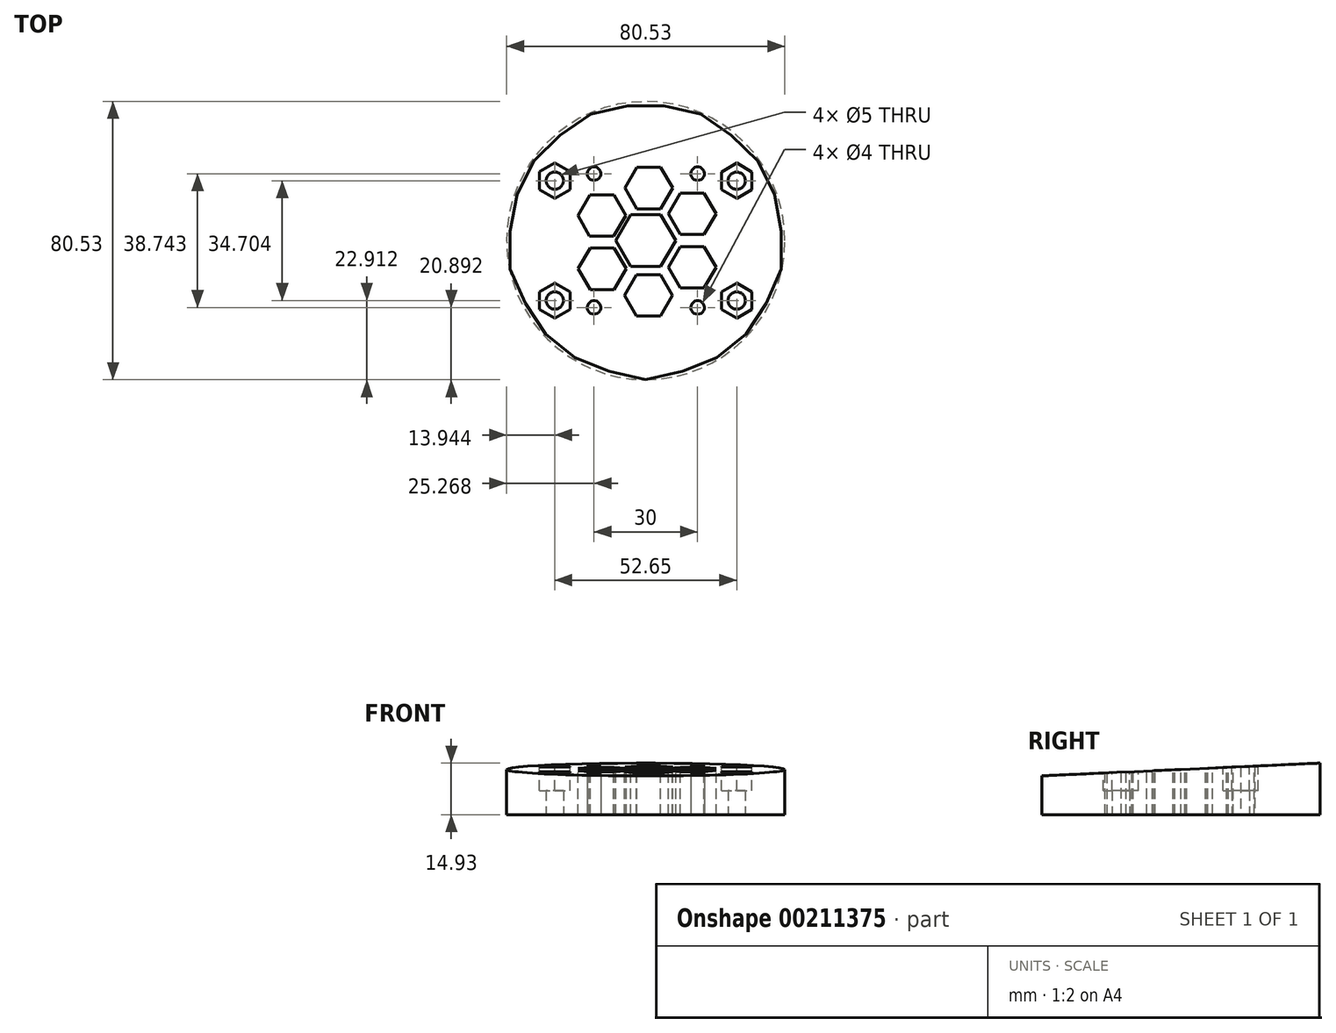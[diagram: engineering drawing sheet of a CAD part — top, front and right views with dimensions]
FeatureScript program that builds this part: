
annotation { "Feature Type Name" : "Feature", "Feature Type Description" : "" }
export const myFeature = defineFeature(function(context is Context, id is Id, definition is map)
    precondition{}
    {
        {
            var Q0;
            Q0=qCreatedBy(makeId("Top.planeOp"),FACE);
            var sketch = newSketch(context, id + "F0", { "sketchPlane" : qUnion([Q0])});
            skLineSegment(sketch, "E0", {"start": v(-26.5, 26.43) * mm, "end": v(3.5, -12.3) * mm, "construction": true});
            skLineSegment(sketch, "E1", {"start": v(-26.5, -12.3) * mm, "end": v(3.5, 26.43) * mm, "construction": true});
            skLineSegment(sketch, "E2", {"start": v(-47.1, 26.43) * mm, "end": v(43.2, 26.43) * mm, "construction": true});
            skLineSegment(sketch, "E3", {"start": v(3.5, -12.3) * mm, "end": v(-78.64, -12.3) * mm, "construction": true});
            skCircle(sketch, "E4", {"center": v(-26.5, 26.43) * mm, "radius": 2 * mm});
            skCircle(sketch, "E5", {"center": v(3.5, 26.43) * mm, "radius": 2 * mm});
            skCircle(sketch, "E6", {"center": v(3.5, -12.3) * mm, "radius": 2 * mm});
            skCircle(sketch, "E7", {"center": v(-26.5, -12.3) * mm, "radius": 2 * mm});
            skCircle(sketch, "E8", {"center": v(-11.5, 7.06) * mm, "radius": 40.27 * mm});
            skSolve(sketch);
        }
        {
            var Q0;
            Q0=qCreatedBy(makeId("Top.planeOp"),FACE);
            cPlane(context, id + "F1", {"entities" : qUnion([Q0]), "cplaneType" : CPlaneType.OFFSET, "offset" : 25 * mm, "width" : 150 * mm, "height" : 150 * mm});
        }
        {
            var Q0;
            Q0=makeQuery(id+"F0.imprint","IMPRINT",FACE,{"disambiguationData":[TD([[makeQuery(id+"F0.imprint","IMPRINT",EDGE,{"derivedFrom":sQuery(id+"F0.wireOp",EDGE,"E4")}),-1.0]])]});
            extrude(context, id + "F2", {"entities" : qUnion([Q0]), "depth" : 20 * mm});
        }
        {
            var Q0;
            Q0=qCreatedBy(makeId("Right.planeOp"),FACE);
            var sketch = newSketch(context, id + "F3", { "sketchPlane" : qUnion([Q0])});
            skLineSegment(sketch, "E9", {"start": v(-39.65, 15.95) * mm, "end": v(68.13, 20.88) * mm});
            skLineSegment(sketch, "E10", {"start": v(68.13, 20.88) * mm, "end": v(67.69, 30.5) * mm});
            skLineSegment(sketch, "E11", {"start": v(67.69, 30.5) * mm, "end": v(-43.8, 30.5) * mm});
            skLineSegment(sketch, "E12", {"start": v(-43.8, 30.5) * mm, "end": v(-39.65, 15.95) * mm});
            skSolve(sketch);
        }
        {
            var Q0;
            Q0=makeQuery(id+"F3.imprint","IMPRINT",FACE,{"disambiguationData":[TD([[makeQuery(id+"F3.imprint","IMPRINT",EDGE,{"derivedFrom":sQuery(id+"F3.wireOp",EDGE,"E9")}),1.0]])]});
            extrude(context, id + "F4", {"entities" : qUnion([Q0]), "operationType" : NewBodyOperationType.REMOVE, "endBound" : BoundingType.SYMMETRIC, "oppositeDirection" : true, "depth" : 139.6 * mm});
        }
        {
            var Q0;
            Q0=qCreatedBy(id+"F1.planeOp",FACE);
            var sketch = newSketch(context, id + "F5", { "sketchPlane" : qUnion([Q0])});
            skLineSegment(sketch, "E13", {"start": v(-26.5, 26.43) * mm, "end": v(3.5, -12.3) * mm, "construction": true});
            skLineSegment(sketch, "E14", {"start": v(3.5, -12.3) * mm, "end": v(3.5, 26.43) * mm, "construction": true});
            skLineSegment(sketch, "E15", {"start": v(3.5, 26.43) * mm, "end": v(-26.5, -12.3) * mm, "construction": true});
            skCircle(sketch, "E16.cCircle", {"center": v(-11.5, 7.06) * mm, "radius": 7.5 * mm, "construction": true});
            skLineSegment(sketch, "E16.0", {"start": v(-15.82, 14.56) * mm, "end": v(-7.16, 14.56) * mm});
            skLineSegment(sketch, "E16.1", {"start": v(-7.16, 14.56) * mm, "end": v(-2.83, 7.06) * mm});
            skLineSegment(sketch, "E16.2", {"start": v(-2.83, 7.06) * mm, "end": v(-7.16, -0.44) * mm});
            skLineSegment(sketch, "E16.3", {"start": v(-7.16, -0.44) * mm, "end": v(-15.82, -0.44) * mm});
            skLineSegment(sketch, "E16.4", {"start": v(-15.82, -0.44) * mm, "end": v(-20.15, 7.06) * mm});
            skLineSegment(sketch, "E16.5", {"start": v(-20.15, 7.06) * mm, "end": v(-15.82, 14.56) * mm});
            skPoint(sketch, "E16.0.midPoint", {"position": v(-11.5, 14.56) * mm});
            skLineSegment(sketch, "E17", {"start": v(-5, 10.81) * mm, "end": v(1.93, 14.81) * mm, "construction": true});
            skLineSegment(sketch, "E18", {"start": v(-5, 3.31) * mm, "end": v(1.93, -0.69) * mm, "construction": true});
            skCircle(sketch, "E19.cCircle", {"center": v(1.93, 14.81) * mm, "radius": 6 * mm, "construction": true});
            skLineSegment(sketch, "E19.0", {"start": v(-1.53, 8.81) * mm, "end": v(-5, 14.81) * mm});
            skLineSegment(sketch, "E19.1", {"start": v(-5, 14.81) * mm, "end": v(-1.53, 20.81) * mm});
            skLineSegment(sketch, "E19.2", {"start": v(-1.53, 20.81) * mm, "end": v(5.4, 20.81) * mm});
            skLineSegment(sketch, "E19.3", {"start": v(5.4, 20.81) * mm, "end": v(8.86, 14.81) * mm});
            skLineSegment(sketch, "E19.4", {"start": v(8.86, 14.81) * mm, "end": v(5.4, 8.81) * mm});
            skLineSegment(sketch, "E19.5", {"start": v(5.4, 8.81) * mm, "end": v(-1.53, 8.81) * mm});
            skPoint(sketch, "E19.0.midPoint", {"position": v(-3.26, 11.81) * mm});
            skCircle(sketch, "E20.cCircle", {"center": v(1.93, -0.69) * mm, "radius": 6 * mm, "construction": true});
            skLineSegment(sketch, "E20.0", {"start": v(-5, -0.69) * mm, "end": v(-1.53, 5.31) * mm});
            skLineSegment(sketch, "E20.1", {"start": v(-1.53, 5.31) * mm, "end": v(5.4, 5.31) * mm});
            skLineSegment(sketch, "E20.2", {"start": v(5.4, 5.31) * mm, "end": v(8.86, -0.69) * mm});
            skLineSegment(sketch, "E20.3", {"start": v(8.86, -0.69) * mm, "end": v(5.4, -6.69) * mm});
            skLineSegment(sketch, "E20.4", {"start": v(5.4, -6.69) * mm, "end": v(-1.53, -6.69) * mm});
            skLineSegment(sketch, "E20.5", {"start": v(-1.53, -6.69) * mm, "end": v(-5, -0.69) * mm});
            skPoint(sketch, "E20.0.midPoint", {"position": v(-3.26, 2.31) * mm});
            skLineSegment(sketch, "E21", {"start": v(-11.5, -0.44) * mm, "end": v(-11.5, -8.44) * mm, "construction": true});
            skLineSegment(sketch, "E22", {"start": v(-17.99, 3.31) * mm, "end": v(-24.91, -0.69) * mm, "construction": true});
            skLineSegment(sketch, "E23", {"start": v(-17.99, 10.81) * mm, "end": v(-24.91, 14.81) * mm, "construction": true});
            skCircle(sketch, "E24.cCircle", {"center": v(-10.7, -8.83) * mm, "radius": 6 * mm, "construction": true});
            skLineSegment(sketch, "E24.0", {"start": v(-17.63, -8.83) * mm, "end": v(-14.17, -2.83) * mm});
            skLineSegment(sketch, "E24.1", {"start": v(-14.17, -2.83) * mm, "end": v(-7.24, -2.83) * mm});
            skLineSegment(sketch, "E24.2", {"start": v(-7.24, -2.83) * mm, "end": v(-3.78, -8.83) * mm});
            skLineSegment(sketch, "E24.3", {"start": v(-3.78, -8.83) * mm, "end": v(-7.24, -14.83) * mm});
            skLineSegment(sketch, "E24.4", {"start": v(-7.24, -14.83) * mm, "end": v(-14.17, -14.83) * mm});
            skLineSegment(sketch, "E24.5", {"start": v(-14.17, -14.83) * mm, "end": v(-17.63, -8.83) * mm});
            skPoint(sketch, "E24.0.midPoint", {"position": v(-15.9, -5.83) * mm});
            skCircle(sketch, "E25.cCircle", {"center": v(-24.1, -1.1) * mm, "radius": 6 * mm, "construction": true});
            skLineSegment(sketch, "E25.0", {"start": v(-31.04, -1.1) * mm, "end": v(-27.57, 4.9) * mm});
            skLineSegment(sketch, "E25.1", {"start": v(-27.57, 4.9) * mm, "end": v(-20.64, 4.9) * mm});
            skLineSegment(sketch, "E25.2", {"start": v(-20.64, 4.9) * mm, "end": v(-17.18, -1.1) * mm});
            skLineSegment(sketch, "E25.3", {"start": v(-17.18, -1.1) * mm, "end": v(-20.64, -7.1) * mm});
            skLineSegment(sketch, "E25.4", {"start": v(-20.64, -7.1) * mm, "end": v(-27.57, -7.1) * mm});
            skLineSegment(sketch, "E25.5", {"start": v(-27.57, -7.1) * mm, "end": v(-31.04, -1.1) * mm});
            skPoint(sketch, "E25.0.midPoint", {"position": v(-29.3, 1.9) * mm});
            skCircle(sketch, "E26.cCircle", {"center": v(-24.22, 14.32) * mm, "radius": 6 * mm, "construction": true});
            skLineSegment(sketch, "E26.0", {"start": v(-31.15, 14.38) * mm, "end": v(-27.64, 20.35) * mm});
            skLineSegment(sketch, "E26.1", {"start": v(-27.64, 20.35) * mm, "end": v(-20.71, 20.3) * mm});
            skLineSegment(sketch, "E26.2", {"start": v(-20.71, 20.3) * mm, "end": v(-17.3, 14.27) * mm});
            skLineSegment(sketch, "E26.3", {"start": v(-17.3, 14.27) * mm, "end": v(-20.8, 8.3) * mm});
            skLineSegment(sketch, "E26.4", {"start": v(-20.8, 8.3) * mm, "end": v(-27.73, 8.35) * mm});
            skLineSegment(sketch, "E26.5", {"start": v(-27.73, 8.35) * mm, "end": v(-31.15, 14.38) * mm});
            skPoint(sketch, "E26.0.midPoint", {"position": v(-29.4, 17.36) * mm});
            skLineSegment(sketch, "E27", {"start": v(-11.5, 14.56) * mm, "end": v(-11.5, 22.56) * mm, "construction": true});
            skCircle(sketch, "E28.cCircle", {"center": v(-10.62, 22.28) * mm, "radius": 6 * mm, "construction": true});
            skLineSegment(sketch, "E28.0", {"start": v(-17.55, 22.28) * mm, "end": v(-14.09, 28.28) * mm});
            skLineSegment(sketch, "E28.1", {"start": v(-14.09, 28.28) * mm, "end": v(-7.16, 28.28) * mm});
            skLineSegment(sketch, "E28.2", {"start": v(-7.16, 28.28) * mm, "end": v(-3.7, 22.28) * mm});
            skLineSegment(sketch, "E28.3", {"start": v(-3.7, 22.28) * mm, "end": v(-7.16, 16.28) * mm});
            skLineSegment(sketch, "E28.4", {"start": v(-7.16, 16.28) * mm, "end": v(-14.09, 16.28) * mm});
            skLineSegment(sketch, "E28.5", {"start": v(-14.09, 16.28) * mm, "end": v(-17.55, 22.28) * mm});
            skPoint(sketch, "E28.0.midPoint", {"position": v(-15.82, 25.28) * mm});
            skLineSegment(sketch, "E29", {"start": v(-11.5, 7.06) * mm, "end": v(-29.5, 7.2) * mm, "construction": true});
            skLineSegment(sketch, "E30", {"start": v(-11.5, 7.06) * mm, "end": v(-11.5, 12.01) * mm, "construction": true});
            skSolve(sketch);
        }
        {
            var Q0;
            Q0=makeQuery(id+"F5.imprint","IMPRINT",FACE,{"disambiguationData":[TD([[makeQuery(id+"F5.imprint","IMPRINT",EDGE,{"derivedFrom":sQuery(id+"F5.wireOp",EDGE,"E19.0")}),-1.0]])]});
            var Q1;
            Q1=makeQuery(id+"F5.imprint","IMPRINT",FACE,{"disambiguationData":[TD([[makeQuery(id+"F5.imprint","IMPRINT",EDGE,{"derivedFrom":sQuery(id+"F5.wireOp",EDGE,"E20.0")}),-1.0]])]});
            var Q2;
            Q2=makeQuery(id+"F5.imprint","IMPRINT",FACE,{"disambiguationData":[TD([[makeQuery(id+"F5.imprint","IMPRINT",EDGE,{"derivedFrom":sQuery(id+"F5.wireOp",EDGE,"E24.0")}),-1.0]])]});
            var Q3;
            Q3=makeQuery(id+"F5.imprint","IMPRINT",FACE,{"disambiguationData":[TD([[makeQuery(id+"F5.imprint","IMPRINT",EDGE,{"derivedFrom":sQuery(id+"F5.wireOp",EDGE,"E25.0")}),-1.0]])]});
            var Q4;
            Q4=makeQuery(id+"F5.imprint","IMPRINT",FACE,{"disambiguationData":[TD([[makeQuery(id+"F5.imprint","IMPRINT",EDGE,{"derivedFrom":sQuery(id+"F5.wireOp",EDGE,"E16.0")}),-1.0]])]});
            var Q5;
            Q5=makeQuery(id+"F5.imprint","IMPRINT",FACE,{"disambiguationData":[TD([[makeQuery(id+"F5.imprint","IMPRINT",EDGE,{"derivedFrom":sQuery(id+"F5.wireOp",EDGE,"E26.0")}),-1.0]])]});
            var Q6;
            Q6=makeQuery(id+"F5.imprint","IMPRINT",FACE,{"disambiguationData":[TD([[makeQuery(id+"F5.imprint","IMPRINT",EDGE,{"derivedFrom":sQuery(id+"F5.wireOp",EDGE,"E28.0")}),-1.0]])]});
            var Q7;
            Q7=makeQuery(id+"F5.imprint","IMPRINT",FACE,{"disambiguationData":[TD([[makeQuery(id+"F5.imprint","IMPRINT",EDGE,{"derivedFrom":sQuery(id+"F5.wireOp",EDGE,"4c5f7111-e0b7-497c-aa14-eb5f7e9c3b38.0")}),-1.0]])]});
            var Q8;
            Q8=makeQuery(id+"F5.imprint","IMPRINT",FACE,{"disambiguationData":[TD([[makeQuery(id+"F5.imprint","IMPRINT",EDGE,{"derivedFrom":sQuery(id+"F5.wireOp",EDGE,"0144ad1a-5e1e-411f-8a7a-8ff4aa9977e40.MirrorCS")}),1.0]])]});
            extrude(context, id + "F6", {"entities" : qUnion([Q0, Q1, Q2, Q3, Q4, Q5, Q6, Q7, Q8]), "operationType" : NewBodyOperationType.REMOVE, "endBound" : BoundingType.THROUGH_ALL, "oppositeDirection" : true, "depth" : 25 * mm});
        }
        {
            var Q0;
            Q0=makeQuery(id+"F2.opExtrude","CAP_FACE",FACE,{"disambiguationData":[OSD([sQuery(id+"F0.wireOp",EDGE,"E4"),sQuery(id+"F0.wireOp",EDGE,"E5"),sQuery(id+"F0.wireOp",EDGE,"E6"),sQuery(id+"F0.wireOp",EDGE,"E7"),sQuery(id+"F0.wireOp",EDGE,"E8")])],"isStart":true});
            extrude(context, id + "F7", {"entities" : qUnion([Q0]), "operationType" : NewBodyOperationType.REMOVE, "oppositeDirection" : true, "depth" : 5 * mm});
        }
        {
            var Q0;
            Q0=makeQuery(id+"F7.boolean.opBoolean","COPY",FACE,{"derivedFrom":makeQuery(id+"F7.opExtrude","CAP_FACE",FACE,{"disambiguationData":[OSD([sQuery(id+"F0.wireOp",EDGE,"E4"),sQuery(id+"F0.wireOp",EDGE,"E5"),sQuery(id+"F0.wireOp",EDGE,"E6"),sQuery(id+"F0.wireOp",EDGE,"E7"),sQuery(id+"F0.wireOp",EDGE,"E8")])],"isStart":false})});
            var sketch = newSketch(context, id + "F8", { "sketchPlane" : qUnion([Q0])});
            skLineSegment(sketch, "E31", {"start": v(3.5, 12.3) * mm, "end": v(-26.5, -26.43) * mm, "construction": true});
            skLineSegment(sketch, "E32", {"start": v(-26.5, -26.43) * mm, "end": v(3.5, -26.43) * mm, "construction": true});
            skLineSegment(sketch, "E33", {"start": v(3.5, -26.43) * mm, "end": v(-26.5, 12.3) * mm, "construction": true});
            skLineSegment(sketch, "E34.bottom", {"start": v(14.83, 10.29) * mm, "end": v(-37.82, 10.29) * mm, "construction": true});
            skLineSegment(sketch, "E34.top", {"start": v(14.83, -24.42) * mm, "end": v(-37.82, -24.42) * mm, "construction": true});
            skLineSegment(sketch, "E34.left", {"start": v(14.83, 10.29) * mm, "end": v(14.83, -24.4) * mm, "construction": true});
            skLineSegment(sketch, "E34.right", {"start": v(-37.82, 10.29) * mm, "end": v(-37.82, -24.42) * mm, "construction": true});
            skPoint(sketch, "E34.middle", {"position": v(-11.5, -7.06) * mm});
            skCircle(sketch, "E35", {"center": v(14.83, 10.29) * mm, "radius": 2.5 * mm});
            skCircle(sketch, "E36", {"center": v(14.83, -24.4) * mm, "radius": 2.5 * mm});
            skCircle(sketch, "E37", {"center": v(-37.82, -24.42) * mm, "radius": 2.5 * mm});
            skCircle(sketch, "E38", {"center": v(-37.82, 10.29) * mm, "radius": 2.5 * mm});
            skSolve(sketch);
        }
        {
            var Q0;
            Q0=makeQuery(id+"F8.imprint","IMPRINT",FACE,{"disambiguationData":[TD([[makeQuery(id+"F8.imprint","IMPRINT",EDGE,{"derivedFrom":sQuery(id+"F8.wireOp",EDGE,"E35")}),1.0]])]});
            var Q1;
            Q1=makeQuery(id+"F8.imprint","IMPRINT",FACE,{"disambiguationData":[TD([[makeQuery(id+"F8.imprint","IMPRINT",EDGE,{"derivedFrom":sQuery(id+"F8.wireOp",EDGE,"E36")}),1.0]])]});
            var Q2;
            Q2=makeQuery(id+"F8.imprint","IMPRINT",FACE,{"disambiguationData":[TD([[makeQuery(id+"F8.imprint","IMPRINT",EDGE,{"derivedFrom":sQuery(id+"F8.wireOp",EDGE,"E37")}),1.0]])]});
            var Q3;
            Q3=makeQuery(id+"F8.imprint","IMPRINT",FACE,{"disambiguationData":[TD([[makeQuery(id+"F8.imprint","IMPRINT",EDGE,{"derivedFrom":sQuery(id+"F8.wireOp",EDGE,"E38")}),1.0]])]});
            var Q4;
            Q4=sQuery(id+"F8.wireOp",EDGE,"E35");
            var Q5;
            Q5=sQuery(id+"F8.wireOp",EDGE,"E36");
            var Q6;
            Q6=sQuery(id+"F8.wireOp",EDGE,"E37");
            var Q7;
            Q7=sQuery(id+"F8.wireOp",EDGE,"E38");
            extrude(context, id + "F9", {"entities" : qUnion([Q0, Q1, Q2, Q3]), "operationType" : NewBodyOperationType.REMOVE, "surfaceEntities" : qUnion([Q4, Q5, Q6, Q7]), "endBound" : BoundingType.THROUGH_ALL, "oppositeDirection" : true, "depth" : 7 * mm});
        }
        {
            var Q0;
            Q0=qCreatedBy(id+"F1.planeOp",FACE);
            var sketch = newSketch(context, id + "F10", { "sketchPlane" : qUnion([Q0])});
            skCircle(sketch, "E39.cCircle", {"center": v(14.83, -10.29) * mm, "radius": 4.42 * mm, "construction": true});
            skLineSegment(sketch, "E39.0", {"start": v(19.26, -7.73) * mm, "end": v(19.26, -12.84) * mm});
            skLineSegment(sketch, "E39.1", {"start": v(19.26, -12.84) * mm, "end": v(14.83, -15.4) * mm});
            skLineSegment(sketch, "E39.2", {"start": v(14.83, -15.4) * mm, "end": v(10.4, -12.84) * mm});
            skLineSegment(sketch, "E39.3", {"start": v(10.4, -12.84) * mm, "end": v(10.4, -7.73) * mm});
            skLineSegment(sketch, "E39.4", {"start": v(10.4, -7.73) * mm, "end": v(14.83, -5.18) * mm});
            skLineSegment(sketch, "E39.5", {"start": v(14.83, -5.18) * mm, "end": v(19.26, -7.73) * mm});
            skPoint(sketch, "E39.0.midPoint", {"position": v(19.26, -10.29) * mm});
            skCircle(sketch, "E40.cCircle", {"center": v(-37.82, -10.29) * mm, "radius": 4.42 * mm, "construction": true});
            skLineSegment(sketch, "E40.0", {"start": v(-33.4, -7.73) * mm, "end": v(-33.4, -12.84) * mm});
            skLineSegment(sketch, "E40.1", {"start": v(-33.4, -12.84) * mm, "end": v(-37.82, -15.4) * mm});
            skLineSegment(sketch, "E40.2", {"start": v(-37.82, -15.4) * mm, "end": v(-42.24, -12.84) * mm});
            skLineSegment(sketch, "E40.3", {"start": v(-42.24, -12.84) * mm, "end": v(-42.24, -7.73) * mm});
            skLineSegment(sketch, "E40.4", {"start": v(-42.24, -7.73) * mm, "end": v(-37.82, -5.18) * mm});
            skLineSegment(sketch, "E40.5", {"start": v(-37.82, -5.18) * mm, "end": v(-33.4, -7.73) * mm});
            skPoint(sketch, "E40.0.midPoint", {"position": v(-33.4, -10.29) * mm});
            skCircle(sketch, "E41.cCircle", {"center": v(-37.82, 24.42) * mm, "radius": 4.42 * mm, "construction": true});
            skLineSegment(sketch, "E41.0", {"start": v(-33.4, 26.97) * mm, "end": v(-33.4, 21.86) * mm});
            skLineSegment(sketch, "E41.1", {"start": v(-33.4, 21.86) * mm, "end": v(-37.82, 19.3) * mm});
            skLineSegment(sketch, "E41.2", {"start": v(-37.82, 19.3) * mm, "end": v(-42.24, 21.86) * mm});
            skLineSegment(sketch, "E41.3", {"start": v(-42.24, 21.86) * mm, "end": v(-42.24, 26.97) * mm});
            skLineSegment(sketch, "E41.4", {"start": v(-42.24, 26.97) * mm, "end": v(-37.82, 29.53) * mm});
            skLineSegment(sketch, "E41.5", {"start": v(-37.82, 29.53) * mm, "end": v(-33.4, 26.97) * mm});
            skPoint(sketch, "E41.0.midPoint", {"position": v(-33.4, 24.42) * mm});
            skCircle(sketch, "E42.cCircle", {"center": v(14.83, 24.4) * mm, "radius": 4.42 * mm, "construction": true});
            skLineSegment(sketch, "E42.0", {"start": v(19.26, 26.95) * mm, "end": v(19.26, 21.84) * mm});
            skLineSegment(sketch, "E42.1", {"start": v(19.26, 21.84) * mm, "end": v(14.83, 19.28) * mm});
            skLineSegment(sketch, "E42.2", {"start": v(14.83, 19.28) * mm, "end": v(10.4, 21.84) * mm});
            skLineSegment(sketch, "E42.3", {"start": v(10.4, 21.84) * mm, "end": v(10.4, 26.95) * mm});
            skLineSegment(sketch, "E42.4", {"start": v(10.4, 26.95) * mm, "end": v(14.83, 29.5) * mm});
            skLineSegment(sketch, "E42.5", {"start": v(14.83, 29.5) * mm, "end": v(19.26, 26.95) * mm});
            skPoint(sketch, "E42.0.midPoint", {"position": v(19.26, 24.4) * mm});
            skSolve(sketch);
        }
        {
            var Q0;
            Q0=makeQuery(id+"F10.imprint","IMPRINT",FACE,{"disambiguationData":[TD([[makeQuery(id+"F10.imprint","IMPRINT",EDGE,{"derivedFrom":sQuery(id+"F10.wireOp",EDGE,"E39.0")}),-1.0]])]});
            var Q1;
            Q1=makeQuery(id+"F10.imprint","IMPRINT",FACE,{"disambiguationData":[TD([[makeQuery(id+"F10.imprint","IMPRINT",EDGE,{"derivedFrom":sQuery(id+"F10.wireOp",EDGE,"E42.0")}),-1.0]])]});
            var Q2;
            Q2=makeQuery(id+"F10.imprint","IMPRINT",FACE,{"disambiguationData":[TD([[makeQuery(id+"F10.imprint","IMPRINT",EDGE,{"derivedFrom":sQuery(id+"F10.wireOp",EDGE,"E41.0")}),-1.0]])]});
            var Q3;
            Q3=makeQuery(id+"F10.imprint","IMPRINT",FACE,{"disambiguationData":[TD([[makeQuery(id+"F10.imprint","IMPRINT",EDGE,{"derivedFrom":sQuery(id+"F10.wireOp",EDGE,"E40.0")}),-1.0]])]});
            extrude(context, id + "F11", {"entities" : qUnion([Q0, Q1, Q2, Q3]), "operationType" : NewBodyOperationType.REMOVE, "oppositeDirection" : true, "depth" : 13 * mm});
        }
    });
